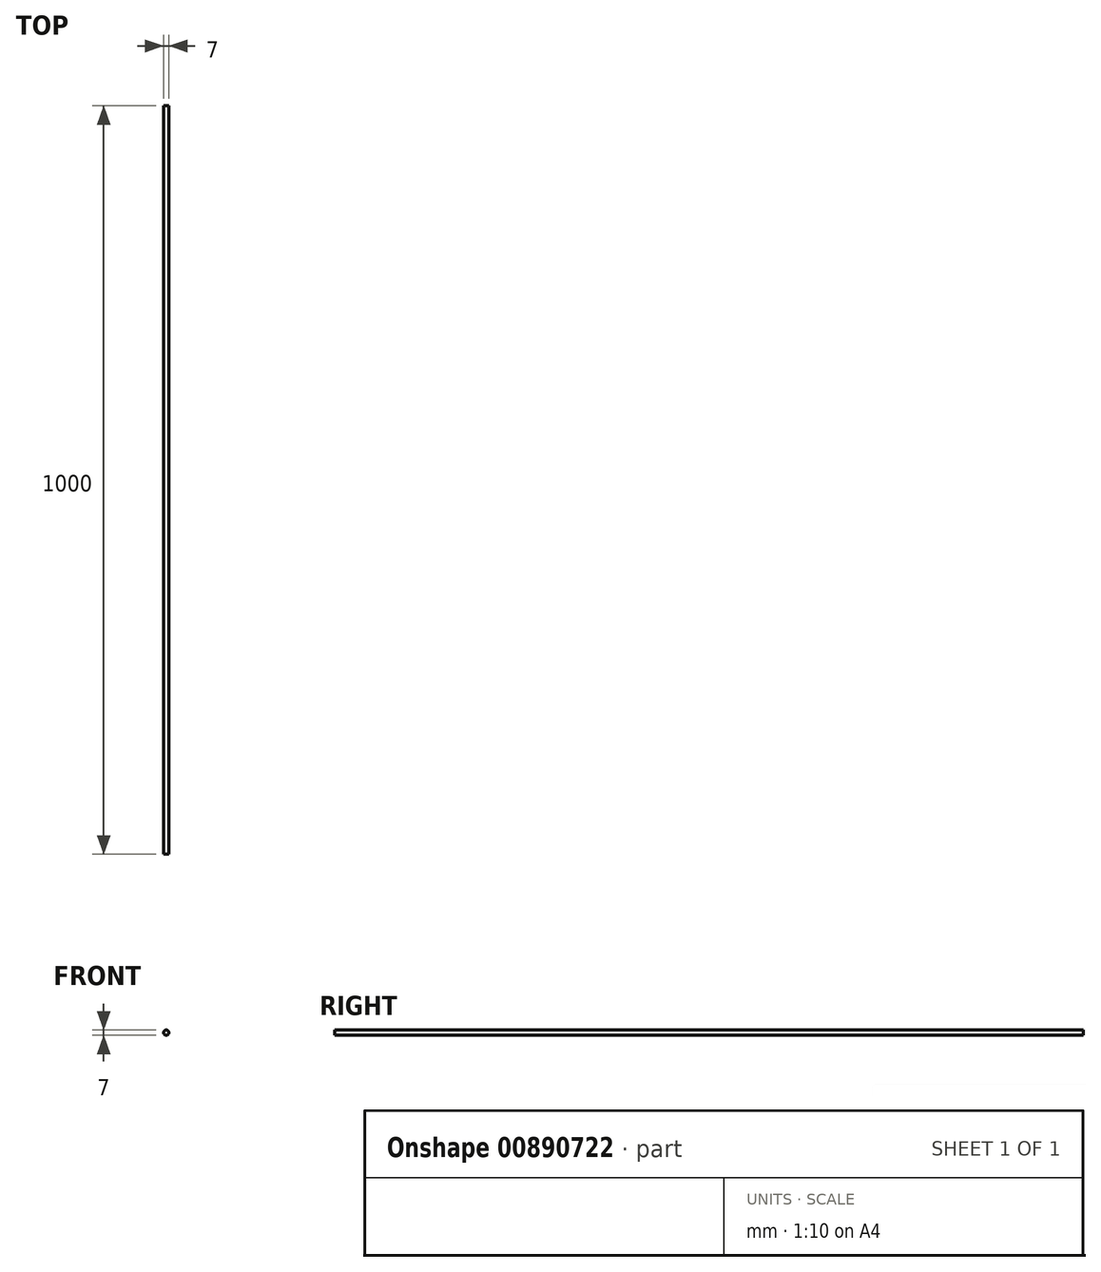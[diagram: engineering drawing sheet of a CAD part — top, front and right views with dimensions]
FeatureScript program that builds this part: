
annotation { "Feature Type Name" : "Feature", "Feature Type Description" : "" }
export const myFeature = defineFeature(function(context is Context, id is Id, definition is map)
    precondition{}
    {
        {
            var Q0;
            Q0=qCreatedBy(makeId("Top.planeOp"),FACE);
            var sketch = newSketch(context, id + "F0", { "sketchPlane" : qUnion([Q0])});
            skLineSegment(sketch, "E0", {"start": v(0, 0) * mm, "end": v(0, 1000) * mm});
            skSolve(sketch);
        }
        {
            var Q0;
            Q0=qCreatedBy(makeId("Front.planeOp"),FACE);
            var sketch = newSketch(context, id + "F1", { "sketchPlane" : qUnion([Q0])});
            skCircle(sketch, "E1", {"center": v(0, 0) * mm, "radius": 3.5 * mm});
            skSolve(sketch);
        }
        {
            var Q0;
            Q0=makeQuery(id+"F1.imprint","IMPRINT",FACE,{"disambiguationData":[TD([[makeQuery(id+"F1.imprint","IMPRINT",EDGE,{"derivedFrom":sQuery(id+"F1.wireOp",EDGE,"E1")}),1.0]])]});
            var Q1;
            Q1=sQuery(id+"F0.wireOp",EDGE,"E0");
            sweep(context, id + "F2", {"profiles" : qUnion([Q0]), "path" : qUnion([Q1])});
        }
    });
